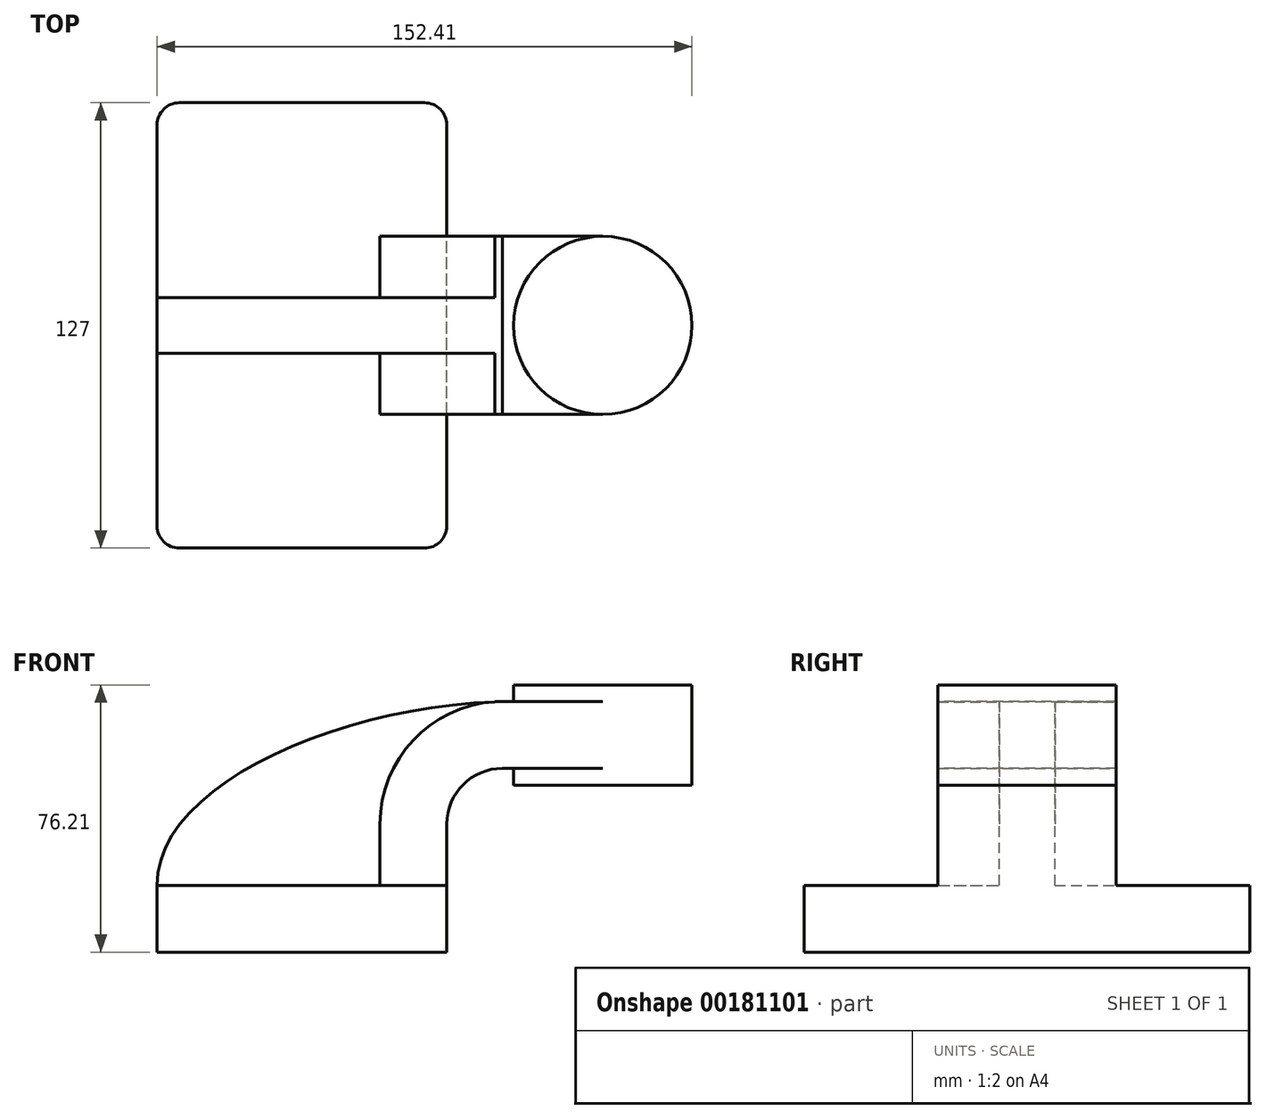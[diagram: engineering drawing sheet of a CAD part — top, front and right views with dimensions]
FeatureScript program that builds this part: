
annotation { "Feature Type Name" : "Feature", "Feature Type Description" : "" }
export const myFeature = defineFeature(function(context is Context, id is Id, definition is map)
    precondition{}
    {
        {
            var Q0;
            Q0=qCreatedBy(makeId("Front.planeOp"),FACE);
            var sketch = newSketch(context, id + "F0", { "sketchPlane" : qUnion([Q0])});
            skLineSegment(sketch, "E0.bottom", {"start": v(41.28, -9.52) * mm, "end": v(-41.28, -9.53) * mm});
            skLineSegment(sketch, "E0.top", {"start": v(41.27, 9.53) * mm, "end": v(-41.28, 9.53) * mm});
            skLineSegment(sketch, "E0.left", {"start": v(41.28, -9.52) * mm, "end": v(41.28, 9.53) * mm});
            skLineSegment(sketch, "E0.right", {"start": v(-41.28, -9.53) * mm, "end": v(-41.28, 9.53) * mm});
            skPoint(sketch, "E0.middle", {"position": v(0, 0) * mm});
            skLineSegment(sketch, "E1.bottom", {"start": v(111.12, 38.1) * mm, "end": v(60.32, 38.1) * mm});
            skLineSegment(sketch, "E1.top", {"start": v(111.12, 66.68) * mm, "end": v(60.32, 66.68) * mm});
            skLineSegment(sketch, "E1.left", {"start": v(111.12, 38.1) * mm, "end": v(111.12, 66.68) * mm});
            skLineSegment(sketch, "E1.right", {"start": v(60.32, 38.1) * mm, "end": v(60.32, 66.67) * mm});
            skPoint(sketch, "E1.middle", {"position": v(85.72, 52.39) * mm});
            skLineSegment(sketch, "E2", {"start": v(41.27, 9.53) * mm, "end": v(41.27, 27) * mm});
            skArc(sketch, "E3", {"start": v(41.27, 27) * mm, "mid": v(45.92, 38.23) * mm, "end": v(57.15, 42.88) * mm});
            skArc(sketch, "E4.1", {"start": v(22.23, 27) * mm, "mid": v(32.45, 51.7) * mm, "end": v(57.15, 61.93) * mm});
            skLineSegment(sketch, "E4.2", {"start": v(22.22, 9.53) * mm, "end": v(22.22, 27) * mm});
            skLineSegment(sketch, "E5", {"start": v(85.72, 66.68) * mm, "end": v(85.72, 38.1) * mm});
            skLineSegment(sketch, "E6", {"start": v(57.15, 61.93) * mm, "end": v(85.72, 61.93) * mm});
            skLineSegment(sketch, "E7", {"start": v(57.15, 42.88) * mm, "end": v(85.72, 42.88) * mm});
            skFitSpline(sketch, "E8", {"points": [v(-41.28, 9.53) * mm, v(57.15, 61.93) * mm], "startDerivative": vector(-0.78, 86.06) * mm, "endDerivative": vector(138.55, 3.36) * mm});
            skSolve(sketch);
        }
        {
            var Q0;
            Q0=makeQuery(id+"F0.imprint","IMPRINT",FACE,{"disambiguationData":[TD([[makeQuery(id+"F0.imprint","IMPRINT",EDGE,{"derivedFrom":sQuery(id+"F0.wireOp",EDGE,"E0.bottom")}),-1.0]])]});
            extrude(context, id + "F1", {"entities" : qUnion([Q0]), "endBound" : BoundingType.SYMMETRIC, "depth" : 127 * mm});
        }
        {
            var Q0;
            {var subQ1=sQuery(id+"F0.wireOp",EDGE,"E2");Q0=makeQuery(id+"F0.imprint","IMPRINT",FACE,{"disambiguationData":[TD([[makeQuery(id+"F0.imprint","IMPRINT",EDGE,{"derivedFrom":subQ1}),1.0]])]});}
            var Q1;
            {var subQ0=sQuery(id+"F0.wireOp",EDGE,"E7");var subQ1=sQuery(id+"F0.wireOp",EDGE,"E1.right");var subQ2=makeQuery(id+"F0.imprint","INTERSECT",VERTEX,{"derivedFrom":[subQ1,subQ0]});Q1=makeQuery(id+"F0.imprint","IMPRINT",FACE,{"disambiguationData":[TD([[makeQuery(id+"F0.imprint","IMPRINT",EDGE,{"disambiguationData":[TD([[subQ2,-1.0]])],"derivedFrom":subQ1}),-1.0]])]});}
            extrude(context, id + "F2", {"entities" : qUnion([Q0, Q1]), "operationType" : NewBodyOperationType.ADD, "endBound" : BoundingType.SYMMETRIC, "depth" : 50.8 * mm});
        }
        {
            var Q0;
            {var subQ3=sQuery(id+"F0.wireOp",EDGE,"E4.2");Q0=makeQuery(id+"F0.imprint","IMPRINT",FACE,{"disambiguationData":[TD([[makeQuery(id+"F0.imprint","IMPRINT",EDGE,{"derivedFrom":subQ3}),1.0]])]});}
            extrude(context, id + "F3", {"entities" : qUnion([Q0]), "operationType" : NewBodyOperationType.ADD, "endBound" : BoundingType.SYMMETRIC, "depth" : 15.88 * mm});
        }
        {
            var Q0;
            {var subQ4=sQuery(id+"F0.wireOp",EDGE,"E1.left");Q0=makeQuery(id+"F0.imprint","IMPRINT",FACE,{"disambiguationData":[TD([[makeQuery(id+"F0.imprint","IMPRINT",EDGE,{"derivedFrom":subQ4}),1.0]])]});}
            var Q1;
            Q1=sQuery(id+"F0.wireOp",EDGE,"E5");
            revolve(context, id + "F4", {"operationType" : NewBodyOperationType.ADD, "entities" : qUnion([Q0]), "axis" : qUnion([Q1]), "revolveType" : RevolveType.FULL});
        }
        {
            var Q0;
            Q0=makeQuery(id+"F1.opExtrude","CAP_EDGE",EDGE,{"disambiguationData":[OSD([sQuery(id+"F0.wireOp",EDGE,"E0.right")])],"isStart":false});
            var Q1;
            Q1=makeQuery(id+"F1.opExtrude","CAP_EDGE",EDGE,{"disambiguationData":[OSD([sQuery(id+"F0.wireOp",EDGE,"E0.left")])],"isStart":false});
            var Q2;
            Q2=makeQuery(id+"F1.opExtrude","CAP_EDGE",EDGE,{"disambiguationData":[OSD([sQuery(id+"F0.wireOp",EDGE,"E0.left")])],"isStart":true});
            var Q3;
            Q3=makeQuery(id+"F1.opExtrude","CAP_EDGE",EDGE,{"disambiguationData":[OSD([sQuery(id+"F0.wireOp",EDGE,"E0.right")])],"isStart":true});
            fillet(context, id + "F5", {"entities" : qUnion([Q0, Q1, Q2, Q3]), "radius" : 6.35 * mm, "tangentPropagation" : true, "allowEdgeOverflow" : false});
        }
    });
